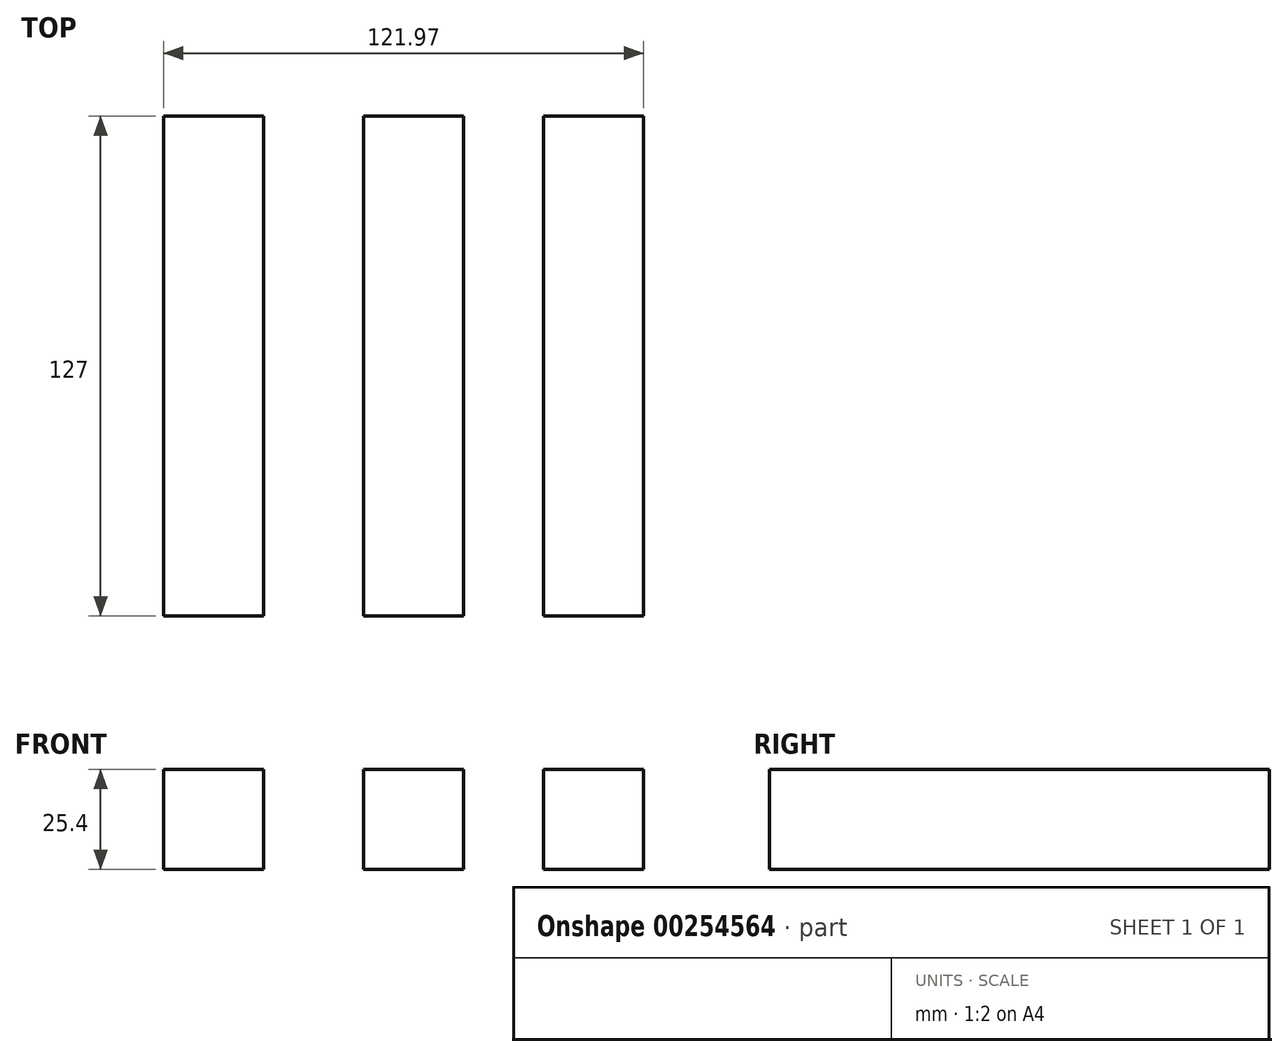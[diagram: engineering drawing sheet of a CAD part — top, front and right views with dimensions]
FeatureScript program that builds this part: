
annotation { "Feature Type Name" : "Feature", "Feature Type Description" : "" }
export const myFeature = defineFeature(function(context is Context, id is Id, definition is map)
    precondition{}
    {
        {
            var Q0;
            Q0=qCreatedBy(makeId("Front.planeOp"),FACE);
            var sketch = newSketch(context, id + "F0", { "sketchPlane" : qUnion([Q0])});
            skLineSegment(sketch, "E0.bottom", {"start": v(0, 0) * mm, "end": v(25.4, 0) * mm});
            skLineSegment(sketch, "E0.top", {"start": v(0, 25.4) * mm, "end": v(25.4, 25.4) * mm});
            skLineSegment(sketch, "E0.left", {"start": v(0, 0) * mm, "end": v(0, 25.4) * mm});
            skLineSegment(sketch, "E0.right", {"start": v(25.4, 0) * mm, "end": v(25.4, 25.4) * mm});
            skLineSegment(sketch, "E1.bottom", {"start": v(45.77, 25.4) * mm, "end": v(71.17, 25.4) * mm});
            skLineSegment(sketch, "E1.top", {"start": v(45.77, 0) * mm, "end": v(71.17, 0) * mm});
            skLineSegment(sketch, "E1.left", {"start": v(45.77, 25.4) * mm, "end": v(45.77, 0) * mm});
            skLineSegment(sketch, "E1.right", {"start": v(71.17, 25.4) * mm, "end": v(71.17, 0) * mm});
            skLineSegment(sketch, "E2.bottom", {"start": v(-50.8, 25.4) * mm, "end": v(-25.4, 25.4) * mm});
            skLineSegment(sketch, "E2.top", {"start": v(-50.8, 0) * mm, "end": v(-25.4, 0) * mm});
            skLineSegment(sketch, "E2.left", {"start": v(-50.8, 25.4) * mm, "end": v(-50.8, 0) * mm});
            skLineSegment(sketch, "E2.right", {"start": v(-25.4, 25.4) * mm, "end": v(-25.4, 0) * mm});
            skSolve(sketch);
        }
        {
            var Q0;
            Q0=makeQuery(id+"F0.imprint","IMPRINT",FACE,{"disambiguationData":[TD([[makeQuery(id+"F0.imprint","IMPRINT",EDGE,{"derivedFrom":sQuery(id+"F0.wireOp",EDGE,"E2.bottom")}),-1.0]])]});
            var Q1;
            Q1=makeQuery(id+"F0.imprint","IMPRINT",FACE,{"disambiguationData":[TD([[makeQuery(id+"F0.imprint","IMPRINT",EDGE,{"derivedFrom":sQuery(id+"F0.wireOp",EDGE,"E0.bottom")}),1.0]])]});
            var Q2;
            Q2=makeQuery(id+"F0.imprint","IMPRINT",FACE,{"disambiguationData":[TD([[makeQuery(id+"F0.imprint","IMPRINT",EDGE,{"derivedFrom":sQuery(id+"F0.wireOp",EDGE,"E1.bottom")}),-1.0]])]});
            extrude(context, id + "F1", {"entities" : qUnion([Q0, Q1, Q2]), "endBound" : BoundingType.SYMMETRIC, "depth" : 127 * mm});
        }
    });
